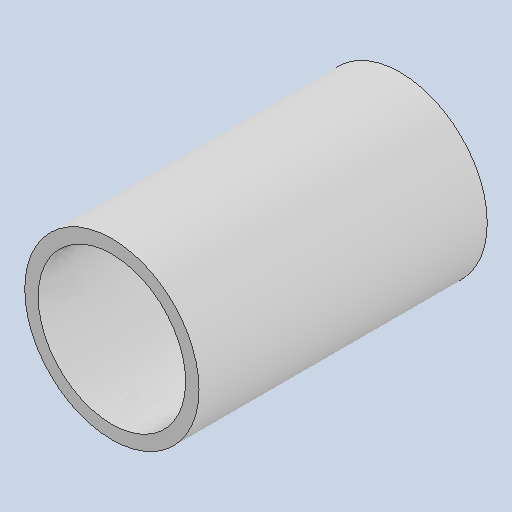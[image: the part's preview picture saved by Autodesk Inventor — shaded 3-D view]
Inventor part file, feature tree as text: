
AUTODESK INVENTOR PART (.ipt)
format: ipt  version: 2023.2 (Build 272271030, 271C)  size: 137,728 bytes
history: native  units: mm
features: extrude x1, sketch x1
ambient origin geometry x8: Origin, YZ Plane, XZ Plane, XY Plane, X Axis, Y Axis, Z Axis, Center Point
bodies: Solid1 (feature_tree)
feature tree (2):
  extrude  "Extrusion1"  Depth=86.0mm
  sketch  "Sketch1"  dims[d0=52.0mm d1=4.0mm d2=86.0mm d3=0.0mm]
